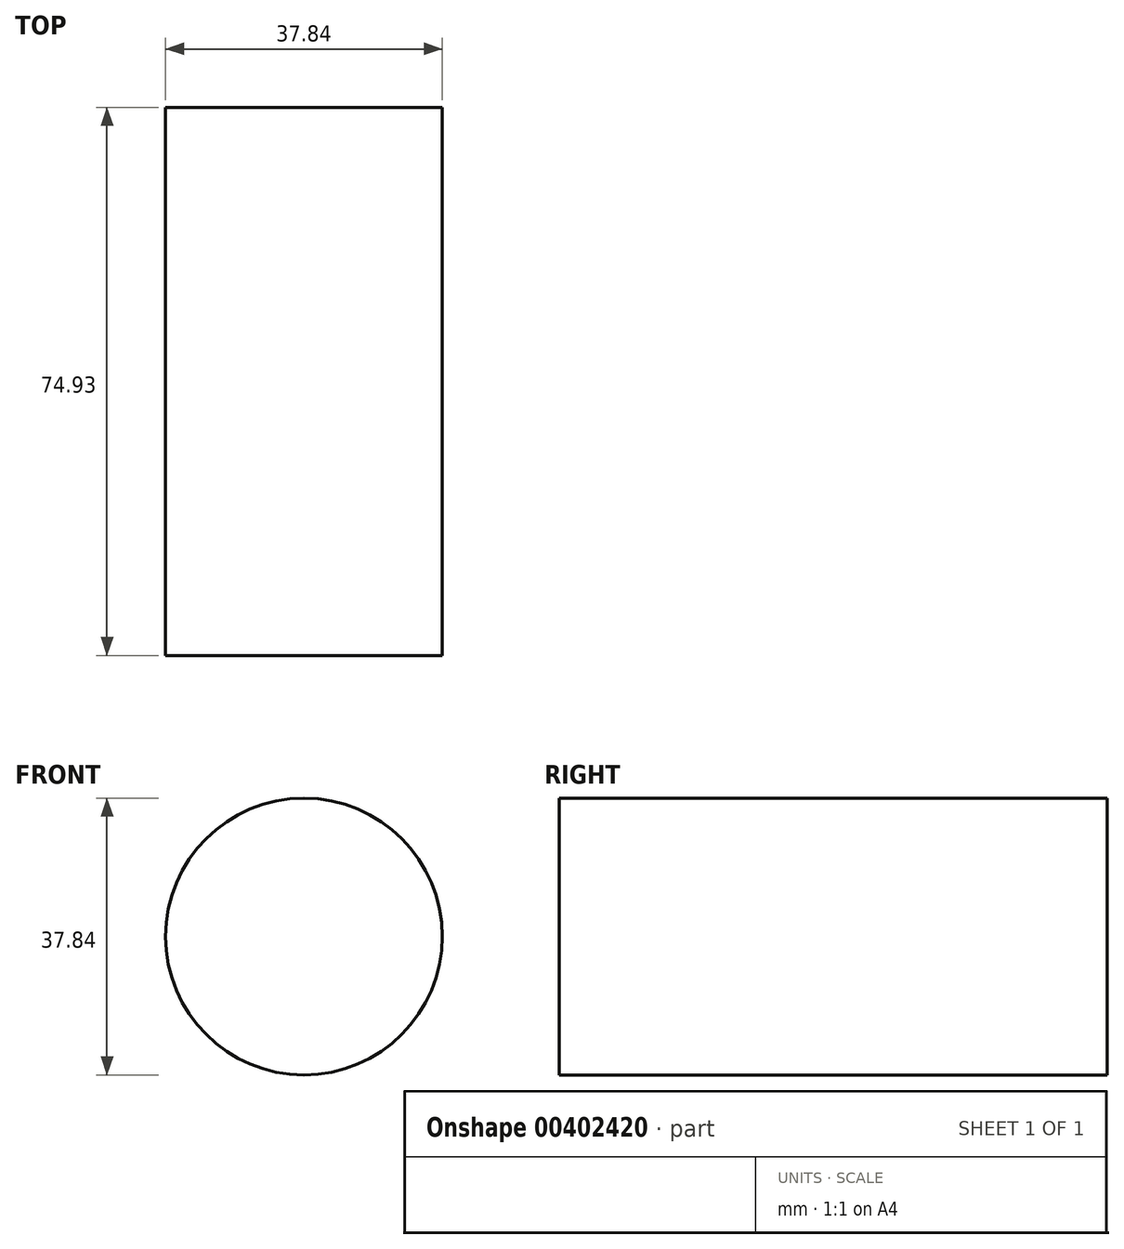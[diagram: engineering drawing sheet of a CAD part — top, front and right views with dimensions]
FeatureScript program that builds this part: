
annotation { "Feature Type Name" : "Feature", "Feature Type Description" : "" }
export const myFeature = defineFeature(function(context is Context, id is Id, definition is map)
    precondition{}
    {
        {
            var Q0;
            Q0=qCreatedBy(makeId("Front.planeOp"),FACE);
            var sketch = newSketch(context, id + "F0", { "sketchPlane" : qUnion([Q0])});
            skCircle(sketch, "E0", {"center": v(0, 0) * mm, "radius": 18.92 * mm});
            skSolve(sketch);
        }
        {
            var Q0;
            Q0=makeQuery(id+"F0.imprint","IMPRINT",FACE,{"disambiguationData":[TD([[makeQuery(id+"F0.imprint","IMPRINT",EDGE,{"derivedFrom":sQuery(id+"F0.wireOp",EDGE,"E0")}),1.0]])]});
            extrude(context, id + "F1", {"entities" : qUnion([Q0]), "depth" : 74.93 * mm});
        }
    });
